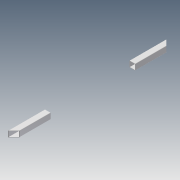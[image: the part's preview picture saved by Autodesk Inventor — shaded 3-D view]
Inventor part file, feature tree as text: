
AUTODESK INVENTOR PART (.ipt)
format: ipt  version: 2014 (Build 180170000, 170)  size: 134,144 bytes
history: native  units: in
note: dims shown in document units (in); Inventor stores cm internally (conversion verified against a paired STEP export)
features: extrude x3, sketch x3
ambient origin geometry x8: Origin, YZ Plane, XZ Plane, XY Plane, X Axis, Y Axis, Z Axis, Center Point
bodies: Solid1 (feature_tree)
feature tree (6):
  extrude  "Extrusion1"  Depth=1.0in
  extrude  "Extrusion2"  Depth=0.063in
  extrude  "Extrusion3"  TaperAngle=45.0deg  [1 undecoded]
  sketch  "Sketch1"  dims[d0=1.0in d1=1.0in]
  sketch  "Sketch2"  dims[d2=0.07in d3=0.063in]
  sketch  "Sketch3"  dims[d4=27.0in d5=0.0in d7=45.0deg d9=45.0deg d10=1.0in d11=0.0in d12=14.45in d13=1.0in d14=0.0in]
note: 1 required parameter value undecoded (feature->parameter linkage not recoverable at this tier; creation-order binding heuristic only, values carry confidence <= 0.55)
